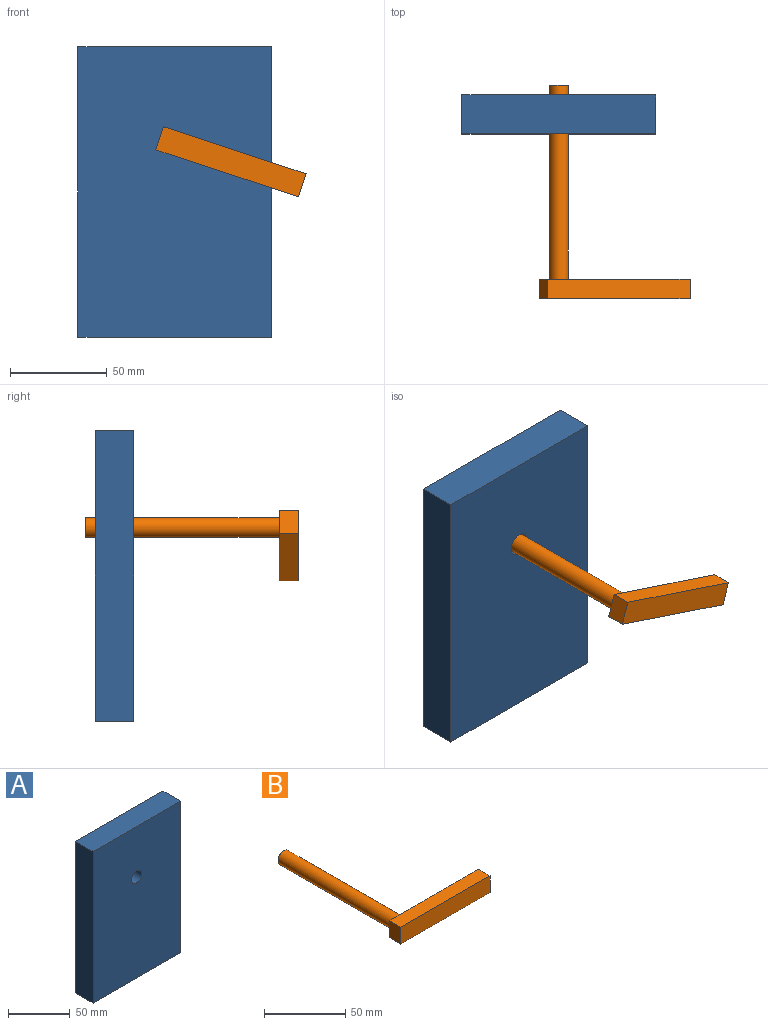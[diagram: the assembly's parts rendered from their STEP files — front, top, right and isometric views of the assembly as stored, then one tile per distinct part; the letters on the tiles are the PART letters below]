
ASSEMBLY  parts=2 mates=2
PART A: 7 faces, bbox 100x20x150 mm
  f0: plane 150x20mm, normal (-1,0,0), area 3000mm2, adj f1,f3,f4,f5
  f1: plane 100x20mm, normal (0,0,-1), area 2000mm2, adj f0,f2,f4,f5
  f2: plane 150x20mm, normal (1,0,0), area 3000mm2, adj f1,f3,f4,f5
  f3: plane 100x20mm, normal (0,0,1), area 2000mm2, adj f0,f2,f4,f5
  f4: plane 150x100mm, normal (0,-1,0), area 14886.9mm2, adj f0,f1,f2,f3,f6
  f5: plane 150x100mm, normal (0,1,0), area 14886.9mm2, adj f0,f1,f2,f3,f6
  f6: cylinder r=6mm len=20mm, axis (0,-1,0), area 754mm2, adj f4,f5
PART B: 8 faces, bbox 77.5x110x12.6 mm
  f0: cylinder r=5mm len=100mm, axis (0,1,0), area 3141.6mm2, adj f1,f7
  f1: plane 10x10mm, normal (0,1,0), area 78.5mm2, adj f0
  f2: plane 12.58x10mm, normal (-1,0,0), area 125.8mm2, adj f3,f5,f6,f7
  f3: plane 77.47x10mm, normal (0,0,-1), area 774.7mm2, adj f2,f4,f6,f7
  f4: plane 12.58x10mm, normal (1,0,0), area 125.8mm2, adj f3,f5,f6,f7
  f5: plane 77.47x10mm, normal (0,0,1), area 774.7mm2, adj f2,f4,f6,f7
  f6: plane 77.47x12.58mm, normal (0,-1,0), area 974.3mm2, adj f2,f3,f4,f5
  f7: plane 77.47x12.58mm, normal (0,1,0), area 895.7mm2, adj f0,f2,f3,f4,f5
PLACE A t=(13.42,151.28,-57.69)mm fixed
PLACE B rot(axis=(0,1,0),18.3deg) t=(12.45,156.28,-24.39)mm
MATE cylindrical B.f0 <-> A.f6  axis (0,1,0) through (12.45,106.28,-24.39)mm
MATE parallel B.f0 <-> A.f5  axis (0,1,0) through (12.45,156.28,-24.39)mm
